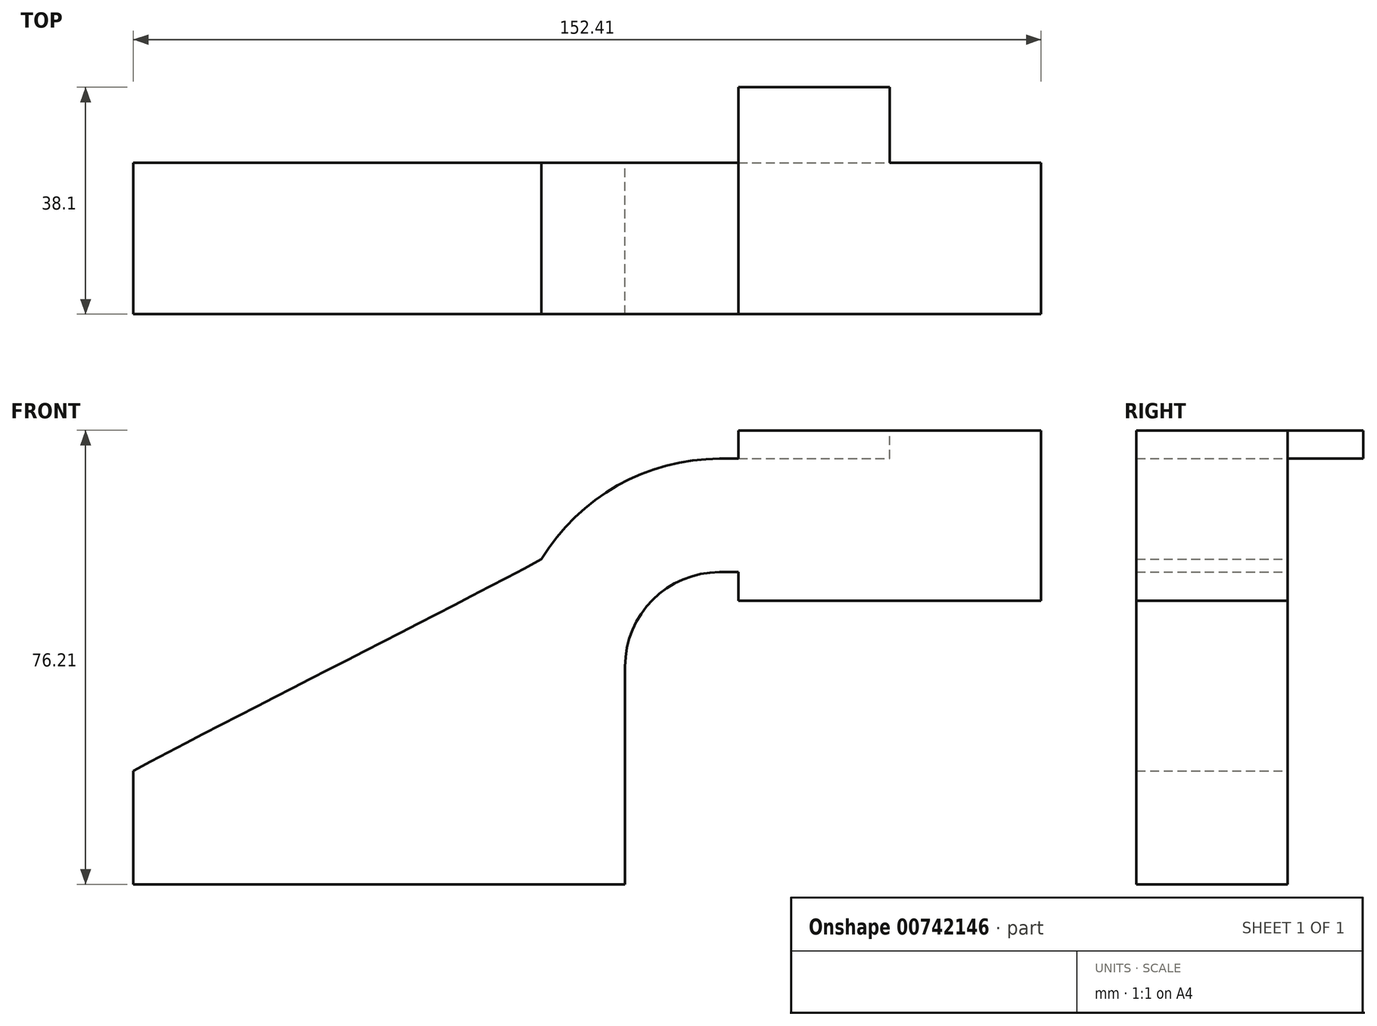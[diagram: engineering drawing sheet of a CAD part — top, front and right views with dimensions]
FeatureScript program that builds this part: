
annotation { "Feature Type Name" : "Feature", "Feature Type Description" : "" }
export const myFeature = defineFeature(function(context is Context, id is Id, definition is map)
    precondition{}
    {
        {
            var Q0;
            Q0=qCreatedBy(makeId("Front.planeOp"),FACE);
            var sketch = newSketch(context, id + "F0", { "sketchPlane" : qUnion([Q0])});
            skLineSegment(sketch, "E0.bottom", {"start": v(-41.28, -9.53) * mm, "end": v(41.28, -9.53) * mm});
            skLineSegment(sketch, "E0.top", {"start": v(-41.28, 9.53) * mm, "end": v(41.28, 9.53) * mm});
            skLineSegment(sketch, "E0.left", {"start": v(-41.28, -9.53) * mm, "end": v(-41.28, 9.53) * mm});
            skLineSegment(sketch, "E0.right", {"start": v(41.28, -9.53) * mm, "end": v(41.28, 9.52) * mm});
            skPoint(sketch, "E0.middle", {"position": v(0, 0) * mm});
            skLineSegment(sketch, "E1.bottom", {"start": v(60.32, 38.1) * mm, "end": v(111.12, 38.1) * mm});
            skLineSegment(sketch, "E1.top", {"start": v(60.32, 66.67) * mm, "end": v(111.12, 66.67) * mm});
            skLineSegment(sketch, "E1.left", {"start": v(60.32, 38.1) * mm, "end": v(60.32, 66.67) * mm});
            skLineSegment(sketch, "E1.right", {"start": v(111.12, 38.1) * mm, "end": v(111.12, 66.68) * mm});
            skPoint(sketch, "E1.middle", {"position": v(85.72, 52.39) * mm});
            skLineSegment(sketch, "E2", {"start": v(41.28, 9.52) * mm, "end": v(41.28, 27) * mm});
            skArc(sketch, "E3", {"start": v(41.27, 27) * mm, "mid": v(45.92, 38.23) * mm, "end": v(57.15, 42.88) * mm});
            skLineSegment(sketch, "E4", {"start": v(57.15, 42.88) * mm, "end": v(85.72, 42.88) * mm});
            skLineSegment(sketch, "E5", {"start": v(-171.48, 29.8) * mm, "end": v(-168.49, 24.23) * mm});
            skLineSegment(sketch, "E6.0", {"start": v(47.63, 9.52) * mm, "end": v(47.63, 27) * mm});
            skLineSegment(sketch, "E7.0", {"start": v(57.15, 61.93) * mm, "end": v(85.72, 61.93) * mm});
            skArc(sketch, "E7.1", {"start": v(22.22, 27) * mm, "mid": v(32.45, 51.7) * mm, "end": v(57.15, 61.93) * mm});
            skLineSegment(sketch, "E7.2", {"start": v(22.22, 9.52) * mm, "end": v(22.22, 27) * mm});
            skLineSegment(sketch, "E8", {"start": v(85.72, 38.1) * mm, "end": v(85.72, 66.67) * mm});
            skFitSpline(sketch, "E9", {"points": [v(-41.28, 9.52) * mm, v(57.15, 61.93) * mm], "startDerivative": vector(98.43, 52.4) * mm, "endDerivative": vector(84.6, 51.6) * mm});
            skSolve(sketch);
        }
        {
            var Q0;
            {var subQ0=sQuery(id+"F0.wireOp",EDGE,"E1.left");var subQ1=sQuery(id+"F0.wireOp",EDGE,"E1.top");var subQ2=makeQuery(id+"F0.imprint","INTERSECT",VERTEX,{"derivedFrom":[subQ1,subQ0]});Q0=makeQuery(id+"F0.imprint","IMPRINT",FACE,{"disambiguationData":[TD([[makeQuery(id+"F0.imprint","IMPRINT",EDGE,{"disambiguationData":[TD([[subQ2,-1.0]])],"derivedFrom":subQ1}),-1.0]])]});}
            extrude(context, id + "F1", {"entities" : qUnion([Q0]), "endBound" : BoundingType.SYMMETRIC, "depth" : 25.4 * mm, "offsetDistance" : 25.4 * mm});
        }
        {
            var Q0;
            Q0 = qSketchRegion(id + "F0", true);
            extrude(context, id + "F2", {"entities" : qUnion([Q0]), "operationType" : NewBodyOperationType.ADD, "depth" : 25.4 * mm, "offsetDistance" : 25.4 * mm});
        }
    });
